FCSTD DOCUMENT  (FreeCAD 0.17R13247 (Git))
Label: EQUIPAMENTO
License: All rights reserved
LicenseURL: http://en.wikipedia.org/wiki/All_rights_reserved
objects: Part::FeaturePython×19, App::FeaturePython×5
note: 19 computed .brp shape members not serialized (recipe doc carries the construction recipe); baked Part::Feature solids carry a one-line shape summary decoded from their .brp

FEATURE [Part::FeaturePython] TAMPA_01  # a2plus imported part (geometry in sourceFile) (typed FeaturePython)
  fixedPosition = true
  sourceFile = <path> - EQUIPAMENTO/TAMPA.FCStd
  timeLastImport = 1.52294e+09
  updateColors = true
FEATURE [Part::FeaturePython] CORPO_01  # a2plus imported part (geometry in sourceFile) (typed FeaturePython)
  Placement = pos=(464,0,-859.6) rot=(0,-1,0;1.5708rad)
  fixedPosition = false
  sourceFile = <path> - EQUIPAMENTO/CORPO.FCStd
  timeLastImport = 1.52294e+09
  updateColors = true
FEATURE [App::FeaturePython] circularEdgeConstraint01  label="circularEdgeConstraint01__TAMPA_01"  # a2plus constraint (typed FeaturePython)
  Object1 = CORPO_01
  Object2 = TAMPA_01
  SubElement1 = Edge98
  SubElement2 = Edge35
  Type = circularEdge
  directionConstraint = 0
  lockRotation = false
  offset = -3
FEATURE [App::FeaturePython] circularEdgeConstraint01_mirror  label="circularEdgeConstraint01__CORPO_01"  # a2plus constraint (typed FeaturePython)
  Object1 = CORPO_01
  Object2 = TAMPA_01
  SubElement1 = Edge98
  SubElement2 = Edge35
  Type = circularEdge
  directionConstraint = 0
  lockRotation = false
  offset = -3
FEATURE [App::FeaturePython] circularEdgeConstraint02_mirror  label="circularEdgeConstraint02__TAMPA_02"  # a2plus constraint (typed FeaturePython)
  Object1 = TAMPA_02
  Object2 = CORPO_01
  SubElement1 = Edge35
  SubElement2 = Edge31
  Type = circularEdge
  directionConstraint = 1
  lockRotation = false
  offset = 3
FEATURE [Part::FeaturePython] Washer  label="M30-Washer"  # Fasteners workbench fastener (typed FeaturePython)
  Placement = pos=(-170.088,-333.816,47.6) rot=(0,0,1;0rad)
  baseObject = -> TAMPA_01 [Edge72]
  diameter = 9
  invert = false
  matchOuter = false
  offset = 0
  type = 1
FEATURE [Part::FeaturePython] Washer001  label="M30-Washer001"  # Fasteners workbench fastener (typed FeaturePython)
  Placement = pos=(-170.088,-333.816,-50.6) rot=(-1,0,0;3.14159rad)
  baseObject = -> CORPO_01 [Edge133]
  diameter = 9
  invert = true
  matchOuter = false
  offset = 0
  type = 1
FEATURE [Part::FeaturePython] Screw  label="M30x150-Screw"  # Fasteners workbench fastener (typed FeaturePython)
  Placement = pos=(-170.088,-333.816,51.9) rot=(0,0,1;0rad)
  baseObject = -> Washer [Edge1]
  diameter = 19
  invert = false
  length = 9
  matchOuter = false
  offset = 0
  thread = false
  type = 14
FEATURE [Part::FeaturePython] Nut  label="M30-Nut"  # Fasteners workbench fastener (typed FeaturePython)
  Placement = pos=(-170.088,-333.816,-54.9) rot=(-1,0,0;3.14159rad)
  baseObject = -> Washer001 [Edge1]
  diameter = 19
  invert = false
  matchOuter = false
  offset = 0
  thread = false
  type = 1
FEATURE [Part::FeaturePython] Array  # Draft array (typed FeaturePython)
  Angle = 360
  ArrayType = 1
  Axis = (0,0,1)
  Base = -> Washer
  Center = (0,0,0)
  Fuse = false
  IntervalAxis = (0,0,0)
  IntervalX = (1,0,0)
  IntervalY = (0,1,0)
  IntervalZ = (0,0,0)
  NumberPolar = 20
  NumberX = 2
  NumberY = 2
  NumberZ = 1
FEATURE [Part::FeaturePython] Array001  # Draft array (typed FeaturePython)
  Angle = 360
  ArrayType = 1
  Axis = (0,0,1)
  Base = -> Washer001
  Center = (0,0,0)
  Fuse = false
  IntervalAxis = (0,0,0)
  IntervalX = (1,0,0)
  IntervalY = (0,1,0)
  IntervalZ = (0,0,0)
  NumberPolar = 20
  NumberX = 2
  NumberY = 2
  NumberZ = 1
FEATURE [Part::FeaturePython] Array002  # Draft array (typed FeaturePython)
  Angle = 360
  ArrayType = 1
  Axis = (0,0,1)
  Base = -> Screw
  Center = (0,0,0)
  Fuse = false
  IntervalAxis = (0,0,0)
  IntervalX = (1,0,0)
  IntervalY = (0,1,0)
  IntervalZ = (0,0,0)
  NumberPolar = 20
  NumberX = 2
  NumberY = 2
  NumberZ = 1
FEATURE [Part::FeaturePython] Array003  # Draft array (typed FeaturePython)
  Angle = 360
  ArrayType = 1
  Axis = (0,0,1)
  Base = -> Nut
  Center = (0,0,0)
  Fuse = false
  IntervalAxis = (0,0,0)
  IntervalX = (1,0,0)
  IntervalY = (0,1,0)
  IntervalZ = (0,0,0)
  NumberPolar = 20
  NumberX = 2
  NumberY = 2
  NumberZ = 1
FEATURE [Part::FeaturePython] Washer002  label="M30-Washer002"  # Fasteners workbench fastener (typed FeaturePython)
  Placement = pos=(-170.088,-333.816,-1951) rot=(0,0,1;0rad)
  baseObject = -> CORPO_01 [Edge68]
  diameter = 9
  invert = false
  matchOuter = false
  offset = 0
  type = 1
FEATURE [Part::FeaturePython] Screw001  label="M30x150-Screw001"  # Fasteners workbench fastener (typed FeaturePython)
  Placement = pos=(-170.088,-333.816,-1946.7) rot=(0,0,1;0rad)
  baseObject = -> Washer002 [Edge1]
  diameter = 19
  invert = false
  length = 9
  matchOuter = false
  offset = 0
  thread = false
  type = 14
FEATURE [Part::FeaturePython] TAMPA_02  # a2plus imported part (geometry in sourceFile) (typed FeaturePython)
  Placement = pos=(0,0,-2001.6) rot=(0,1,0;3.14159rad)
  fixedPosition = false
  sourceFile = <path> - EQUIPAMENTO/TAMPA.FCStd
  timeLastImport = 1.52294e+09
  updateColors = true
FEATURE [App::FeaturePython] circularEdgeConstraint02  label="circularEdgeConstraint02__CORPO_01"  # a2plus constraint (typed FeaturePython)
  Object1 = TAMPA_02
  Object2 = CORPO_01
  SubElement1 = Edge35
  SubElement2 = Edge31
  Type = circularEdge
  directionConstraint = 1
  lockRotation = false
  offset = 3
FEATURE [App::FeaturePython] circularEdgeConstraint02_mirror001  label="circularEdgeConstraint02__TAMPA_003"  # a2plus constraint (typed FeaturePython)
  Object1 = TAMPA_02
  Object2 = CORPO_01
  SubElement1 = Edge35
  SubElement2 = Edge31
  Type = circularEdge
  directionConstraint = 1
  lockRotation = false
  offset = 3
FEATURE [Part::FeaturePython] Washer003  label="M30-Washer003"  # Fasteners workbench fastener (typed FeaturePython)
  Placement = pos=(-170.088,-333.816,-2049.55) rot=(-1,0,0;3.14159rad)
  baseObject = -> Screw001 [Edge39]
  diameter = 9
  invert = true
  matchOuter = false
  offset = -45
  type = 1
FEATURE [Part::FeaturePython] Nut001  label="M30-Nut001"  # Fasteners workbench fastener (typed FeaturePython)
  Placement = pos=(-170.088,-333.816,-2053.85) rot=(-1,0,0;3.14159rad)
  baseObject = -> Washer003 [Edge1]
  diameter = 19
  invert = false
  matchOuter = false
  offset = 0
  thread = false
  type = 1
FEATURE [Part::FeaturePython] Array004  # Draft array (typed FeaturePython)
  Angle = 360
  ArrayType = 1
  Axis = (0,0,1)
  Base = -> Washer002
  Center = (0,0,0)
  Fuse = false
  IntervalAxis = (0,0,0)
  IntervalX = (1,0,0)
  IntervalY = (0,1,0)
  IntervalZ = (0,0,0)
  NumberPolar = 20
  NumberX = 2
  NumberY = 2
  NumberZ = 1
FEATURE [Part::FeaturePython] Array005  # Draft array (typed FeaturePython)
  Angle = 360
  ArrayType = 1
  Axis = (0,0,1)
  Base = -> Washer003
  Center = (0,0,0)
  Fuse = false
  IntervalAxis = (0,0,0)
  IntervalX = (1,0,0)
  IntervalY = (0,1,0)
  IntervalZ = (0,0,0)
  NumberPolar = 20
  NumberX = 2
  NumberY = 2
  NumberZ = 1
FEATURE [Part::FeaturePython] Array006  # Draft array (typed FeaturePython)
  Angle = 360
  ArrayType = 1
  Axis = (0,0,1)
  Base = -> Screw001
  Center = (0,0,0)
  Fuse = false
  IntervalAxis = (0,0,0)
  IntervalX = (1,0,0)
  IntervalY = (0,1,0)
  IntervalZ = (0,0,0)
  NumberPolar = 20
  NumberX = 2
  NumberY = 2
  NumberZ = 1
FEATURE [Part::FeaturePython] Array007  # Draft array (typed FeaturePython)
  Angle = 360
  ArrayType = 1
  Axis = (0,0,1)
  Base = -> Nut001
  Center = (0,0,0)
  Fuse = false
  IntervalAxis = (0,0,0)
  IntervalX = (1,0,0)
  IntervalY = (0,1,0)
  IntervalZ = (0,0,0)
  NumberPolar = 20
  NumberX = 2
  NumberY = 2
  NumberZ = 1
note: 3 file-system paths scrubbed to <path> (originals preserved in the JSON sidecar)
